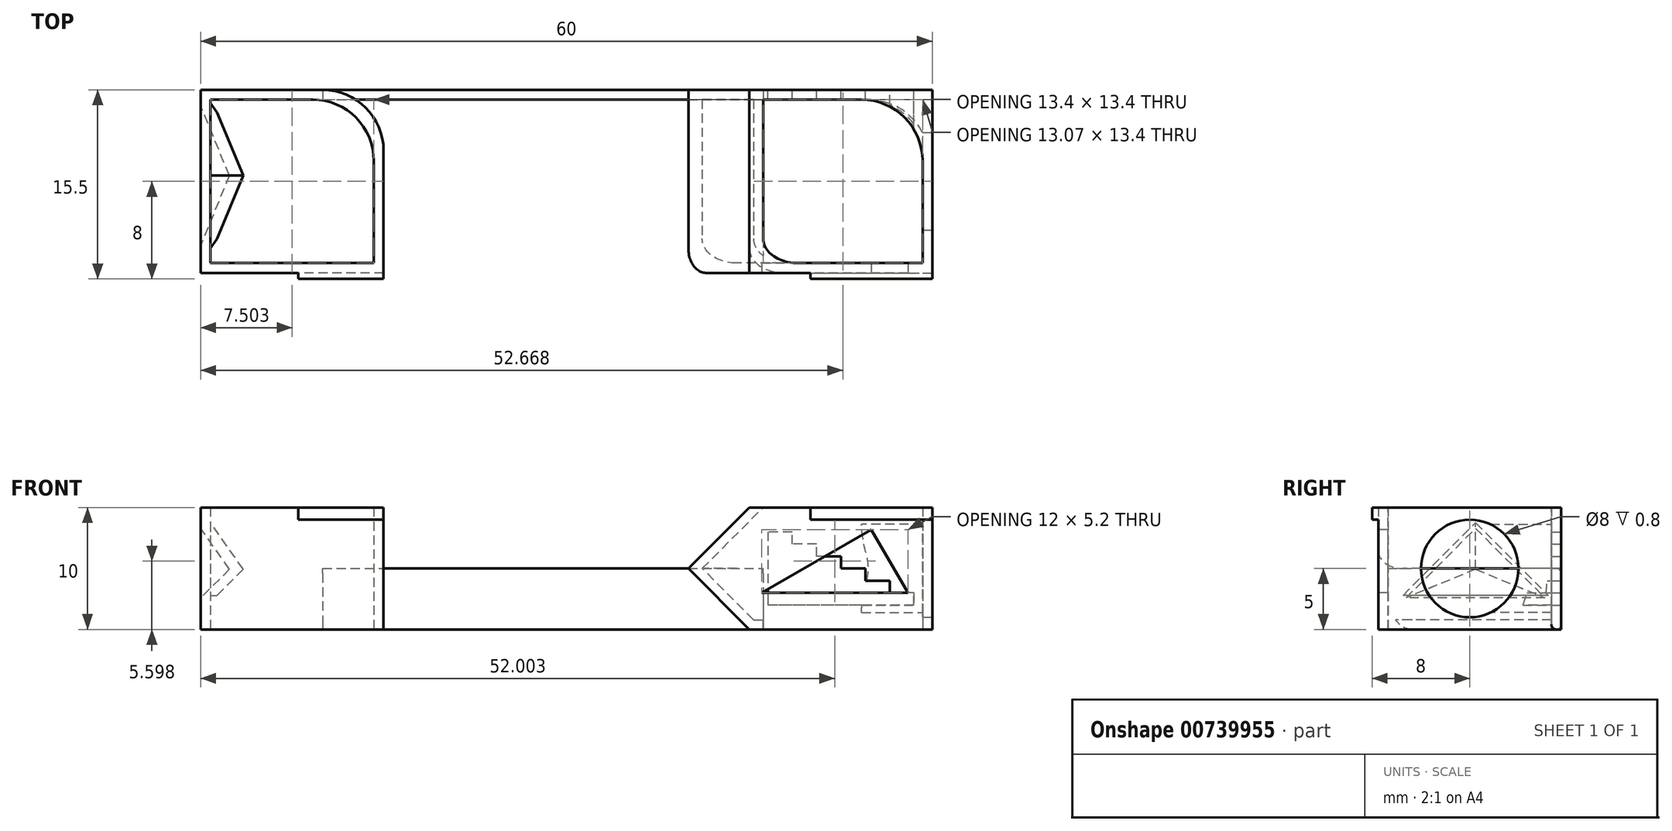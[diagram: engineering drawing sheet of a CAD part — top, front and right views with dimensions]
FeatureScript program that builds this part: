
annotation { "Feature Type Name" : "Feature", "Feature Type Description" : "" }
export const myFeature = defineFeature(function(context is Context, id is Id, definition is map)
    precondition{}
    {
        {
            var Q0;
            Q0=qCreatedBy(makeId("Top.planeOp"),FACE);
            var sketch = newSketch(context, id + "F0", { "sketchPlane" : qUnion([Q0])});
            skLineSegment(sketch, "E0.bottom", {"start": v(-5.53, 15) * mm, "end": v(9.47, 15) * mm});
            skLineSegment(sketch, "E0.top", {"start": v(-5.53, 0) * mm, "end": v(9.47, 0) * mm});
            skLineSegment(sketch, "E0.left", {"start": v(-5.53, 15) * mm, "end": v(-5.53, 0) * mm});
            skLineSegment(sketch, "E0.right", {"start": v(9.47, 15) * mm, "end": v(9.47, 0) * mm});
            skLineSegment(sketch, "E1.bottom", {"start": v(39.47, 15) * mm, "end": v(54.47, 15) * mm});
            skLineSegment(sketch, "E1.top", {"start": v(39.47, 0) * mm, "end": v(54.47, 0) * mm});
            skLineSegment(sketch, "E1.left", {"start": v(39.47, 15) * mm, "end": v(39.47, 0) * mm});
            skLineSegment(sketch, "E1.right", {"start": v(54.47, 15) * mm, "end": v(54.47, 0) * mm});
            skSolve(sketch);
        }
        {
            var Q0;
            Q0=qSketchRegion(id+"F0",true);
            extrude(context, id + "F1", {"entities" : qUnion([Q0]), "depth" : 10 * mm, "offsetDistance" : 25 * mm});
        }
        {
            var Q0;
            Q0=makeQuery(id+"F1.opExtrude","SWEPT_FACE",FACE,{"disambiguationData":[OSD([sQuery(id+"F0.wireOp",EDGE,"E0.left")])]});
            var sketch = newSketch(context, id + "F2", { "sketchPlane" : qUnion([Q0])});
            skLineSegment(sketch, "E2", {"start": v(-13.67, 2.59) * mm, "end": v(-7.98, 8.28) * mm});
            skLineSegment(sketch, "E3", {"start": v(-7.98, 8.28) * mm, "end": v(-2.28, 2.59) * mm});
            skLineSegment(sketch, "E4", {"start": v(-2.28, 2.59) * mm, "end": v(-13.67, 2.59) * mm});
            skSolve(sketch);
        }
        {
            var Q0;
            Q0=makeQuery(id+"F2.imprint","IMPRINT",FACE,{"disambiguationData":[TD([[makeQuery(id+"F2.imprint","IMPRINT",EDGE,{"derivedFrom":sQuery(id+"F2.wireOp",EDGE,"smF5woDr-yULW-UryL-FCjF-wCC1mkTt3jYH")}),-1.0]])]});
            var Q1;
            Q1=makeQuery(id+"F2.imprint","IMPRINT",FACE,{"disambiguationData":[TD([[makeQuery(id+"F2.imprint","IMPRINT",EDGE,{"derivedFrom":sQuery(id+"F2.wireOp",EDGE,"E2")}),-1.0]])]});
            extrude(context, id + "F3", {"entities" : qUnion([Q0, Q1]), "operationType" : NewBodyOperationType.REMOVE, "oppositeDirection" : true, "depth" : 10 * mm, "offsetDistance" : 25 * mm, "hasDraft" : true, "draftAngle" : 45 * degree, "draftPullDirection" : true});
        }
        {
            var Q0;
            Q0=makeQuery(id+"F1.opExtrude","SWEPT_FACE",FACE,{"disambiguationData":[OSD([sQuery(id+"F0.wireOp",EDGE,"E1.top")])]});
            var sketch = newSketch(context, id + "F4", { "sketchPlane" : qUnion([Q0])});
            skLineSegment(sketch, "E5", {"start": v(39.47, 0) * mm, "end": v(34.47, 5) * mm});
            skLineSegment(sketch, "E6", {"start": v(34.47, 5) * mm, "end": v(39.47, 10) * mm});
            skLineSegment(sketch, "E7", {"start": v(39.47, 10) * mm, "end": v(39.47, 0) * mm});
            skSolve(sketch);
        }
        {
            var Q0;
            Q0=qSketchRegion(id+"F4",true);
            extrude(context, id + "F5", {"entities" : qUnion([Q0]), "operationType" : NewBodyOperationType.ADD, "oppositeDirection" : true, "depth" : 15 * mm, "offsetDistance" : 25 * mm});
        }
        {
            var Q0;
            Q0=makeQuery(id+"F1.opExtrude","CAP_FACE",FACE,{"disambiguationData":[OSD([sQuery(id+"F0.wireOp",EDGE,"E0.bottom"),sQuery(id+"F0.wireOp",EDGE,"E0.top"),sQuery(id+"F0.wireOp",EDGE,"E0.left"),sQuery(id+"F0.wireOp",EDGE,"E0.right")])],"isStart":false});
            var Q1;
            Q1=makeQuery(id+"F1.opExtrude","CAP_FACE",FACE,{"disambiguationData":[OSD([sQuery(id+"F0.wireOp",EDGE,"E1.bottom"),sQuery(id+"F0.wireOp",EDGE,"E1.top"),sQuery(id+"F0.wireOp",EDGE,"E1.left"),sQuery(id+"F0.wireOp",EDGE,"E1.right")])],"isStart":false});
            shell(context, id + "F6", {"entities" : qUnion([Q0, Q1]), "thickness" : 0.8 * mm});
        }
        {
            var Q0;
            Q0=makeQuery(id+"F6.opShell","OFFSET_FACE",FACE,{"disambiguationData":[OSD([sQuery(id+"F0.wireOp",EDGE,"E0.bottom"),sQuery(id+"F0.wireOp",EDGE,"E0.top"),sQuery(id+"F0.wireOp",EDGE,"E0.left"),sQuery(id+"F0.wireOp",EDGE,"E0.right")])]});
            var sketch = newSketch(context, id + "F7", { "sketchPlane" : qUnion([Q0])});
            skLineSegment(sketch, "E8.0.0", {"start": v(-4.73, 14.2) * mm, "end": v(-4.73, 0.8) * mm});
            skLineSegment(sketch, "E8.0.1", {"start": v(-4.73, 0.8) * mm, "end": v(8.67, 0.8) * mm});
            skLineSegment(sketch, "E8.0.2", {"start": v(8.67, 0.8) * mm, "end": v(8.67, 14.2) * mm});
            skLineSegment(sketch, "E8.0.3", {"start": v(8.67, 14.2) * mm, "end": v(-4.73, 14.2) * mm});
            skSolve(sketch);
        }
        {
            var Q0;
            Q0=qSketchRegion(id+"F7",true);
            extrude(context, id + "F8", {"entities" : qUnion([Q0]), "operationType" : NewBodyOperationType.REMOVE, "endBound" : BoundingType.SYMMETRIC, "oppositeDirection" : true, "depth" : 4 * mm, "offsetDistance" : 25 * mm});
        }
        {
            var Q0;
            Q0=makeQuery(id+"F6.opShell","OFFSET_FACE",FACE,{"disambiguationData":[OSD([sQuery(id+"F0.wireOp",EDGE,"E1.bottom"),sQuery(id+"F0.wireOp",EDGE,"E1.top"),sQuery(id+"F0.wireOp",EDGE,"E1.left"),sQuery(id+"F0.wireOp",EDGE,"E1.right")])]});
            var sketch = newSketch(context, id + "F9", { "sketchPlane" : qUnion([Q0])});
            skLineSegment(sketch, "E9.0", {"start": v(40.6, 14.2) * mm, "end": v(53.67, 14.2) * mm});
            skLineSegment(sketch, "E10.0", {"start": v(40.6, 14.2) * mm, "end": v(40.6, 0.8) * mm});
            skLineSegment(sketch, "E11.0", {"start": v(40.6, 0.8) * mm, "end": v(53.67, 0.8) * mm});
            skLineSegment(sketch, "E12.0", {"start": v(53.67, 14.2) * mm, "end": v(53.67, 0.8) * mm});
            skSolve(sketch);
        }
        {
            var Q0;
            Q0=qSketchRegion(id+"F9",true);
            extrude(context, id + "F10", {"entities" : qUnion([Q0]), "operationType" : NewBodyOperationType.REMOVE, "endBound" : BoundingType.SYMMETRIC, "oppositeDirection" : true, "depth" : 5 * mm, "offsetDistance" : 25 * mm});
        }
        {
            var Q0;
            Q0=makeQuery(id+"F1.opExtrude","SWEPT_FACE",FACE,{"disambiguationData":[OSD([sQuery(id+"F0.wireOp",EDGE,"E1.right")])]});
            var sketch = newSketch(context, id + "F11", { "sketchPlane" : qUnion([Q0])});
            skLineSegment(sketch, "E13", {"start": v(0, 10) * mm, "end": v(15, 0) * mm, "construction": true});
            skLineSegment(sketch, "E14", {"start": v(15, 0) * mm, "end": v(0, 0) * mm, "construction": true});
            skLineSegment(sketch, "E15", {"start": v(0, 0) * mm, "end": v(15, 10) * mm, "construction": true});
            skCircle(sketch, "E16", {"center": v(7.5, 5) * mm, "radius": 4 * mm});
            skSolve(sketch);
        }
        {
            var Q0;
            Q0=makeQuery(id+"F11.imprint","IMPRINT",FACE,{"disambiguationData":[TD([[makeQuery(id+"F11.imprint","IMPRINT",EDGE,{"derivedFrom":sQuery(id+"F11.wireOp",EDGE,"E16")}),1.0]])]});
            extrude(context, id + "F12", {"entities" : qUnion([Q0]), "operationType" : NewBodyOperationType.REMOVE, "endBound" : BoundingType.SYMMETRIC, "oppositeDirection" : true, "depth" : 5 * mm, "offsetDistance" : 25 * mm});
        }
        {
            var Q0;
            {var subQ0=sQuery(id+"F4.wireOp",EDGE,"E5");Q0=makeQuery(id+"F6.opShell","OFFSET_EDGE",EDGE,{"disambiguationData":[OSD([subQ0]),TDD([makeQuery(id+"F5.opExtrude","CAP_EDGE",EDGE,{"disambiguationData":[OSD([subQ0])],"isStart":true})])]});}
            var Q1;
            {var subQ0=sQuery(id+"F4.wireOp",EDGE,"E6");Q1=makeQuery(id+"F6.opShell","OFFSET_EDGE",EDGE,{"disambiguationData":[OSD([subQ0]),TDD([makeQuery(id+"F5.opExtrude","CAP_EDGE",EDGE,{"disambiguationData":[OSD([subQ0])],"isStart":true})])]});}
            var Q2;
            Q2=makeQuery(id+"F5.opExtrude","CAP_EDGE",EDGE,{"disambiguationData":[OSD([sQuery(id+"F4.wireOp",EDGE,"E5")])],"isStart":true});
            fillet(context, id + "F13", {"entities" : qUnion([Q0, Q1, Q2]), "radius" : 2 * mm, "tangentPropagation" : true, "allowEdgeOverflow" : false});
        }
        {
            var Q0;
            Q0=makeQuery(id+"F5.boolean.opBoolean","MERGE",FACE,{"derivedFrom":[makeQuery(id+"F1.opExtrude","SWEPT_FACE",FACE,{"disambiguationData":[OSD([sQuery(id+"F0.wireOp",EDGE,"E1.top")])]}),makeQuery(id+"F5.opExtrude","CAP_FACE",FACE,{"disambiguationData":[OSD([sQuery(id+"F4.wireOp",EDGE,"E5"),sQuery(id+"F4.wireOp",EDGE,"E6"),sQuery(id+"F4.wireOp",EDGE,"E7")])],"isStart":true})]});
            var sketch = newSketch(context, id + "F14", { "sketchPlane" : qUnion([Q0])});
            skLineSegment(sketch, "E17", {"start": v(40.47, 3) * mm, "end": v(52.47, 3) * mm});
            skLineSegment(sketch, "E18", {"start": v(52.47, 3) * mm, "end": v(49.47, 8.2) * mm});
            skLineSegment(sketch, "E19", {"start": v(49.47, 8.2) * mm, "end": v(40.47, 3) * mm});
            skSolve(sketch);
        }
        {
            var Q0;
            Q0=qSketchRegion(id+"F14",true);
            extrude(context, id + "F15", {"entities" : qUnion([Q0]), "operationType" : NewBodyOperationType.REMOVE, "endBound" : BoundingType.SYMMETRIC, "oppositeDirection" : true, "depth" : 5 * mm, "offsetDistance" : 25 * mm});
        }
        {
            var Q0;
            Q0=makeQuery(id+"F5.boolean.opBoolean","MERGE",FACE,{"derivedFrom":[makeQuery(id+"F1.opExtrude","SWEPT_FACE",FACE,{"disambiguationData":[OSD([sQuery(id+"F0.wireOp",EDGE,"E1.bottom")])]}),makeQuery(id+"F5.opExtrude","CAP_FACE",FACE,{"disambiguationData":[OSD([sQuery(id+"F4.wireOp",EDGE,"E5"),sQuery(id+"F4.wireOp",EDGE,"E6"),sQuery(id+"F4.wireOp",EDGE,"E7")])],"isStart":false})]});
            var sketch = newSketch(context, id + "F16", { "sketchPlane" : qUnion([Q0])});
            skLineSegment(sketch, "E20.bottom", {"start": v(-52.97, 8) * mm, "end": v(-40.97, 8) * mm});
            skLineSegment(sketch, "E20.top", {"start": v(-52.97, 2) * mm, "end": v(-40.97, 2) * mm});
            skLineSegment(sketch, "E20.left", {"start": v(-52.97, 8) * mm, "end": v(-52.97, 2) * mm});
            skLineSegment(sketch, "E20.right", {"start": v(-40.97, 8) * mm, "end": v(-40.97, 2) * mm});
            skLineSegment(sketch, "E21", {"start": v(-52.97, 3) * mm, "end": v(-50.97, 3) * mm});
            skLineSegment(sketch, "E22", {"start": v(-50.97, 3) * mm, "end": v(-50.97, 4) * mm});
            skLineSegment(sketch, "E23", {"start": v(-50.97, 4) * mm, "end": v(-48.97, 4) * mm});
            skLineSegment(sketch, "E24", {"start": v(-48.97, 4) * mm, "end": v(-48.97, 5) * mm});
            skLineSegment(sketch, "E25", {"start": v(-48.97, 5) * mm, "end": v(-46.97, 5) * mm});
            skLineSegment(sketch, "E26", {"start": v(-46.97, 5) * mm, "end": v(-46.97, 6) * mm});
            skLineSegment(sketch, "E27", {"start": v(-46.97, 6) * mm, "end": v(-44.97, 6) * mm});
            skLineSegment(sketch, "E28", {"start": v(-44.97, 6) * mm, "end": v(-44.97, 7) * mm});
            skLineSegment(sketch, "E29", {"start": v(-44.97, 7) * mm, "end": v(-42.97, 7) * mm});
            skLineSegment(sketch, "E30", {"start": v(-42.97, 7) * mm, "end": v(-42.97, 8) * mm});
            skSolve(sketch);
        }
        {
            var Q0;
            {var subQ4=sQuery(id+"F16.wireOp",EDGE,"E20.top");Q0=makeQuery(id+"F16.imprint","IMPRINT",FACE,{"disambiguationData":[TD([[makeQuery(id+"F16.imprint","IMPRINT",EDGE,{"derivedFrom":subQ4}),1.0]])]});}
            extrude(context, id + "F17", {"entities" : qUnion([Q0]), "operationType" : NewBodyOperationType.REMOVE, "endBound" : BoundingType.SYMMETRIC, "oppositeDirection" : true, "depth" : 4 * mm, "offsetDistance" : 25 * mm});
        }
        {
            var Q0;
            Q0=makeQuery(id+"F10.boolean.opBoolean","MERGE",EDGE,{"derivedFrom":[makeQuery(id+"F6.opShell","OFFSET_EDGE",EDGE,{"disambiguationData":[OSD([sQuery(id+"F0.wireOp",EDGE,"E1.bottom"),sQuery(id+"F0.wireOp",EDGE,"E1.right")])]}),makeQuery(id+"F10.opExtrude","SWEPT_EDGE",EDGE,{"disambiguationData":[OSD([sQuery(id+"F9.wireOp",EDGE,"E9.0"),sQuery(id+"F9.wireOp",EDGE,"E12.0")])]})]});
            var Q1;
            Q1=makeQuery(id+"F1.opExtrude","SWEPT_EDGE",EDGE,{"disambiguationData":[OSD([sQuery(id+"F0.wireOp",EDGE,"E0.bottom"),sQuery(id+"F0.wireOp",EDGE,"E0.right")])]});
            var Q2;
            Q2=makeQuery(id+"F8.boolean.opBoolean","MERGE",EDGE,{"derivedFrom":[makeQuery(id+"F6.opShell","OFFSET_EDGE",EDGE,{"disambiguationData":[OSD([sQuery(id+"F0.wireOp",EDGE,"E0.bottom"),sQuery(id+"F0.wireOp",EDGE,"E0.right")])]}),makeQuery(id+"F8.opExtrude","SWEPT_EDGE",EDGE,{"disambiguationData":[OSD([sQuery(id+"F7.wireOp",EDGE,"E8.0.2"),sQuery(id+"F7.wireOp",EDGE,"E8.0.3")])]})]});
            fillet(context, id + "F18", {"entities" : qUnion([Q0, Q1, Q2]), "radius" : 5 * mm, "tangentPropagation" : true, "allowEdgeOverflow" : false});
        }
        {
            var Q0;
            Q0=makeQuery(id+"F1.opExtrude","SWEPT_FACE",FACE,{"disambiguationData":[OSD([sQuery(id+"F0.wireOp",EDGE,"E0.top")])]});
            var sketch = newSketch(context, id + "F19", { "sketchPlane" : qUnion([Q0])});
            skLineSegment(sketch, "E31.bottom", {"start": v(9.47, 10) * mm, "end": v(2.47, 10) * mm});
            skLineSegment(sketch, "E31.top", {"start": v(9.47, 9) * mm, "end": v(2.47, 9) * mm});
            skLineSegment(sketch, "E31.left", {"start": v(9.47, 10) * mm, "end": v(9.47, 9) * mm});
            skLineSegment(sketch, "E31.right", {"start": v(2.47, 10) * mm, "end": v(2.47, 9) * mm});
            skSolve(sketch);
        }
        {
            var Q0;
            Q0=qSketchRegion(id+"F19",true);
            extrude(context, id + "F20", {"entities" : qUnion([Q0]), "operationType" : NewBodyOperationType.ADD, "endBound" : BoundingType.SYMMETRIC, "depth" : 1 * mm, "offsetDistance" : 25 * mm});
        }
        {
            var Q0;
            Q0=makeQuery(id+"F5.boolean.opBoolean","MERGE",FACE,{"derivedFrom":[makeQuery(id+"F1.opExtrude","SWEPT_FACE",FACE,{"disambiguationData":[OSD([sQuery(id+"F0.wireOp",EDGE,"E1.top")])]}),makeQuery(id+"F5.opExtrude","CAP_FACE",FACE,{"disambiguationData":[OSD([sQuery(id+"F4.wireOp",EDGE,"E5"),sQuery(id+"F4.wireOp",EDGE,"E6"),sQuery(id+"F4.wireOp",EDGE,"E7")])],"isStart":true})]});
            var sketch = newSketch(context, id + "F21", { "sketchPlane" : qUnion([Q0])});
            skLineSegment(sketch, "E32.bottom", {"start": v(44.47, 10) * mm, "end": v(54.47, 10) * mm});
            skLineSegment(sketch, "E32.top", {"start": v(44.47, 9) * mm, "end": v(54.47, 9) * mm});
            skLineSegment(sketch, "E32.left", {"start": v(44.47, 10) * mm, "end": v(44.47, 9) * mm});
            skLineSegment(sketch, "E32.right", {"start": v(54.47, 10) * mm, "end": v(54.47, 9) * mm});
            skSolve(sketch);
        }
        {
            var Q0;
            Q0=makeQuery(id+"F21.imprint","IMPRINT",FACE,{"disambiguationData":[TD([[makeQuery(id+"F21.imprint","IMPRINT",EDGE,{"derivedFrom":sQuery(id+"F21.wireOp",EDGE,"E32.bottom")}),-1.0]])]});
            extrude(context, id + "F22", {"entities" : qUnion([Q0]), "operationType" : NewBodyOperationType.ADD, "endBound" : BoundingType.SYMMETRIC, "depth" : 1 * mm, "offsetDistance" : 25 * mm});
        }
        {
            var Q0;
            Q0=qCreatedBy(makeId("Top.planeOp"),FACE);
            var sketch = newSketch(context, id + "F23", { "sketchPlane" : qUnion([Q0])});
            skLineSegment(sketch, "E33.bottom", {"start": v(4.47, 14.2) * mm, "end": v(40.6, 14.2) * mm});
            skLineSegment(sketch, "E33.top", {"start": v(4.47, 15) * mm, "end": v(40.6, 15) * mm});
            skLineSegment(sketch, "E33.left", {"start": v(4.47, 14.2) * mm, "end": v(4.47, 15) * mm});
            skLineSegment(sketch, "E33.right", {"start": v(40.6, 14.2) * mm, "end": v(40.6, 15) * mm});
            skSolve(sketch);
        }
        {
            var Q0;
            Q0=makeQuery(id+"F23.imprint","IMPRINT",FACE,{"disambiguationData":[TD([[makeQuery(id+"F23.imprint","IMPRINT",EDGE,{"derivedFrom":sQuery(id+"F23.wireOp",EDGE,"E33.bottom")}),1.0]])]});
            extrude(context, id + "F24", {"entities" : qUnion([Q0]), "depth" : 5 * mm, "offsetDistance" : 25 * mm});
        }
        {
            var Q0;
            Q0=makeQuery(id+"F24.opExtrude","CAP_EDGE",EDGE,{"disambiguationData":[OSD([sQuery(id+"F23.wireOp",EDGE,"E33.top")])],"isStart":false});
            var Q1;
            Q1=makeQuery(id+"F24.opExtrude","CAP_EDGE",EDGE,{"disambiguationData":[OSD([sQuery(id+"F23.wireOp",EDGE,"E33.top")])],"isStart":true});
            var Q2;
            Q2=makeQuery(id+"F24.opExtrude","CAP_EDGE",EDGE,{"disambiguationData":[OSD([sQuery(id+"F23.wireOp",EDGE,"E33.bottom")])],"isStart":true});
            var Q3;
            Q3=makeQuery(id+"F24.opExtrude","CAP_EDGE",EDGE,{"disambiguationData":[OSD([sQuery(id+"F23.wireOp",EDGE,"E33.bottom")])],"isStart":false});
            fillet(context, id + "F25", {"entities" : qUnion([Q0, Q1, Q2, Q3]), "radius" : 0.4 * mm, "tangentPropagation" : true, "allowEdgeOverflow" : false});
        }
    });
